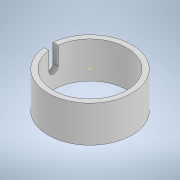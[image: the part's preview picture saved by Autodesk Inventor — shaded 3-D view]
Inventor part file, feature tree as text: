
AUTODESK INVENTOR PART (.ipt)
format: ipt  version: 2022.1 (Build 261234000, 234)  size: 122,880 bytes
history: native  units: in
note: dims shown in document units (in); Inventor stores cm internally (conversion verified against a paired STEP export)
features: sketch x5, extrude x2
ambient origin geometry x8: Origin, YZ Plane, XZ Plane, XY Plane, X Axis, Y Axis, Z Axis, Center Point
bodies: Solid1 (feature_tree)
feature tree (7):
  extrude  "Extrusion1"  Depth=1.01in
  sketch  "3D Sketch1"
  sketch  "3D Sketch2"
  sketch  "Sketch2"  dims[d2=0.5in d3=0.0in d4=0.125in]
  extrude  "Extrusion2"  Depth=0.125in
  sketch  "Sketch1"  dims[d0=1.15in d1=1.01in]
  sketch  "Sketch3"  dims[d5=0.25in d6=0.75in d7=0.0in d8=0.5in d9=0.0344in d10=0.5in d11=0.0344in]
